# Revit family: IS_ConnectFreedom_E6075_BIM_DE
name_source: partatom
category: Plumbing Fixtures
revit_build: Autodesk Revit MEP 2016 (Build: 20161004_0715(x64)
units: mm (PartAtom-declared; Revit-internal decimal feet)

## family parameters
Always vertical = No
Cut with Voids When Loaded = No
OmniClass Number = 23.45.05.21.11.11
OmniClass Title = Water Operated Water Closets
Part Type = Normal
Room Calculation Point = No
Round Connector Dimension = Use Diameter
Shared = No
Work Plane-Based = No

## types (2) — shared parameters
Accessories = www.idealstandard.de\ersatzteile
AssetType = Fixed
BIMobject category = Toilets
BOSUseNativeGeometries = 1
Brand = Ideal Standard
Brand url = http://www.idealstandard.de
CodePerformance = DIN EN 997 CL1-6AC/5A+CLZ, DIN EN
ConnectionType = Plumbing
CurrencyUnit = €
CurrentRevision = 1
Date of publishing = 20/12/2017
DurationUnit = Year
Edition number = 1
ExpectedLife = 25
IFC Classification = Sanitary Terminal
IfcExportAs = IfcSanitaryTerminalType
Installation instructions = http://www.idealstandard.de
InstallationInstructions = www.idealstandard.de\produkte
MaintenanceInformation = www.idealstandard.de\produkte
Manufacturer name = Ideal Standard
ManufacturerURL = http://www.idealstandard.de
Material = Vitreous china
Material main = Ceramics
NBS Reference Code = 35-93-94
NBS Reference Description = Wc Pans
NettWeight = 33.9 Kg
Nominal height = 400
Nominal width = 360
NominalDepth = 540 mm  [stored 1.77165 ft]
NominalHeight = 404 mm
NominalLength = 540 mm  [stored 1.77165 ft]
NominalWidth = 361 mm
OmniClass Code = 23-31 19 00
OmniClass Description = Toilets
PanMaterial = Ceramic
Product Guid = 0694e5b5-5811-42de-bfaf-3b0de7103168
Product SKU = E6075
Product data url = https://bimobject.com
Product family = Sanitary
Product group = Bowl
Product name = CONNECT FREEDOM high level wall mounted bowl 360x540mm, wash-down
Product url = http://www.idealstandard.de
ProductInformation = www.idealstandard.de/produkte
QR code = http://bimobject.com
Shape = Sculptured
Size = 404 x 361 x 540mm
Space = Internal
SpareParts = www.idealstandard.de/ersatzteile
Technical description = http://www.idealstandard.de
ToiletType = Washdown
URL = http://www.idealstandard.de
Uniclass 2015 Code = Pr_40_20_93_94
Uniclass 2015 Name = WC pans
Uniclass2015Code = Pr_40_20_93_94
Uniclass2015Title = WC pans
Uniclass2015Version = Products v1.1
Version = 1
VolumeUnits = Litres
Weight Net (Kg) = 33.9
zero-valued in all types: Cost, OutletConnectionSize, SpilloverLevel

## per-type parameters (varying)
| type | BIMObjectName | BarCode | Color | Description | EAN code | Features | Finish | MainColor | Model | ModelNumber | ModelReference | Name |
| E607501 - CONNECT FREEDOM high level wall mounted bowl 360x540mm, wash-down | ISI_IdealStandard_WcPans_ConnectFreedom_E607501 | 5017830451662 | White | IS Wandtiefspül-WC CONNECT FREEDOM, erhöht, 360x540x400mm, Weiß | https://5017830451662 | IS Wandtiefspül-WC CONNECT FREEDOM, erhöht, 360x540x400mm, Weiß | White | White | E607501 | E607501 | IS Wandtiefspül-WC CONNECT FREEDOM, erhöht, 360x540x400mm, Weiß | WcPans_ConnectFreedom_E607501 |
| E6075MA - CONNECT FREEDOM high level wall mounted bowl 360x540mm, wash-down | ISI_IdealStandard_WcPans_ConnectFreedom_E6075MA | 5017830471073 | WHITE IP | IS Wandtiefspül-WC CONNECT FREEDOM, erhöht, 360x540x400mm, Weiß mit IP | https://5017830471073 | IS Wandtiefspül-WC CONNECT FREEDOM, erhöht, 360x540x400mm, Weiß mit IP | WHITE IP | WHITE IP | E6075MA | E6075MA | IS Wandtiefspül-WC CONNECT FREEDOM, erhöht, 360x540x400mm, Weiß mit IP | WcPans_ConnectFreedom_E6075MA |

note: [stored X ft] marks values corroborated as IEEE doubles in the binary element streams (Revit-internal decimal feet)

## geometry (parser evidence)
native form markers: Blend x4, Sweep x1
no freeform markers — native parametric forms only
